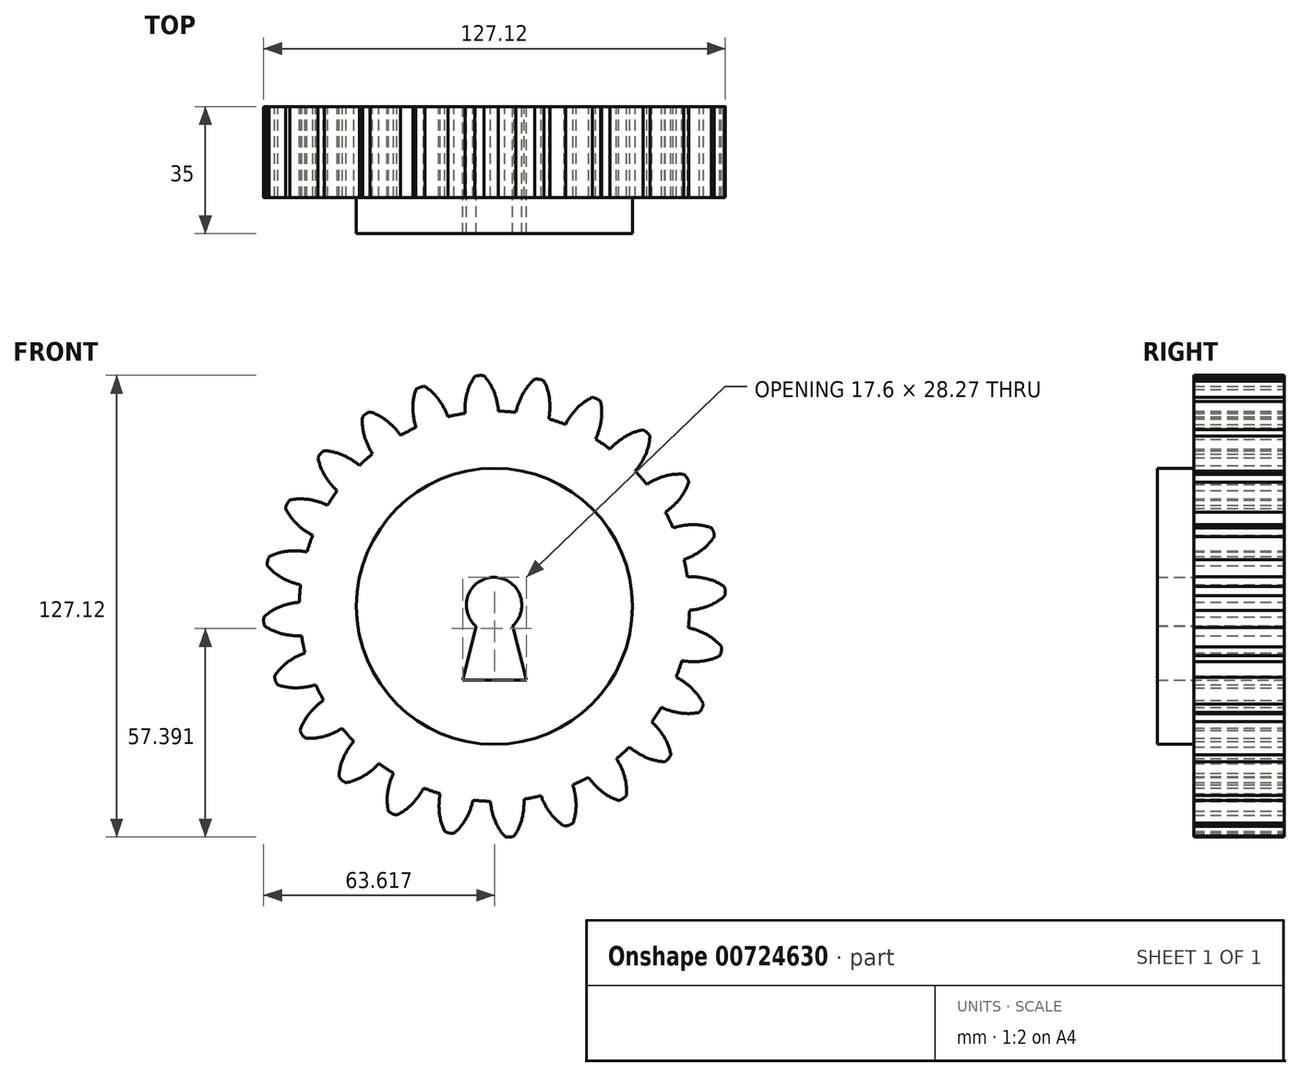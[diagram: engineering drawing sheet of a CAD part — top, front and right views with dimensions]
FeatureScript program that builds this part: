
annotation { "Feature Type Name" : "Feature", "Feature Type Description" : "" }
export const myFeature = defineFeature(function(context is Context, id is Id, definition is map)
    precondition{}
    {
        {
            var Q0;
            Q0=qCreatedBy(makeId("Front.planeOp"),FACE);
            var sketch = newSketch(context, id + "F0", { "sketchPlane" : qUnion([Q0])});
            skCircle(sketch, "E0", {"center": v(0, 0) * mm, "radius": 53.72 * mm});
            skCircle(sketch, "E1", {"center": v(0, 0) * mm, "radius": 58.67 * mm, "construction": true});
            skCircle(sketch, "E2", {"center": v(0, 0) * mm, "radius": 63.5 * mm, "construction": true});
            skLineSegment(sketch, "E3", {"start": v(0, 0) * mm, "end": v(0, 91.84) * mm, "construction": true});
            skLineSegment(sketch, "E4", {"start": v(0, 0) * mm, "end": v(-7.41, 113.09) * mm, "construction": true});
            skLineSegment(sketch, "E5", {"start": v(0, 58.67) * mm, "end": v(-83.5, 56.59) * mm, "construction": true});
            skLineSegment(sketch, "E6", {"start": v(0, 58.67) * mm, "end": v(-75.39, 29.08) * mm, "construction": true});
            skCircle(sketch, "E7", {"center": v(0, 0) * mm, "radius": 54.62 * mm, "construction": true});
            skCircle(sketch, "E8", {"center": v(0, 58.67) * mm, "radius": 16.52 * mm, "construction": true});
            skCircle(sketch, "E9", {"center": v(-15.38, 52.64) * mm, "radius": 16.52 * mm, "construction": true});
            skArc(sketch, "E10", {"start": v(0, 58.67) * mm, "mid": v(-1.21, 61.19) * mm, "end": v(-2.87, 63.43) * mm});
            skArc(sketch, "E11", {"start": v(1.1, 53.7) * mm, "mid": v(0.72, 56.23) * mm, "end": v(0, 58.67) * mm});
            skArc(sketch, "E12.MirrorCS", {"start": v(-8.1, 53.1) * mm, "mid": v(-8.06, 55.65) * mm, "end": v(-7.66, 58.17) * mm});
            skArc(sketch, "E13.MirrorCS", {"start": v(-7.66, 58.17) * mm, "mid": v(-6.78, 60.82) * mm, "end": v(-5.43, 63.27) * mm});
            skArc(sketch, "E14", {"start": v(-2.87, 63.43) * mm, "mid": v(-4.17, 63.55) * mm, "end": v(-5.43, 63.27) * mm});
            skCircle(sketch, "E15", {"center": v(-0.1, 0.31) * mm, "radius": 7.65 * mm});
            skLineSegment(sketch, "E16", {"start": v(-5.08, -5.5) * mm, "end": v(-8.74, -20.3) * mm});
            skLineSegment(sketch, "E17", {"start": v(-8.74, -20.3) * mm, "end": v(8.86, -20.3) * mm});
            skLineSegment(sketch, "E18", {"start": v(8.86, -20.3) * mm, "end": v(5.03, -5.36) * mm});
            skCircle(sketch, "E19", {"center": v(0, 0) * mm, "radius": 38.01 * mm});
            skSolve(sketch);
        }
        {
            var Q0;
            Q0=makeQuery(id+"F0.imprint","IMPRINT",FACE,{"disambiguationData":[TD([[makeQuery(id+"F0.imprint","IMPRINT",EDGE,{"derivedFrom":sQuery(id+"F0.wireOp",EDGE,"E19")}),-1.0]])]});
            var Q1;
            Q1=makeQuery(id+"F0.imprint","IMPRINT",FACE,{"disambiguationData":[TD([[makeQuery(id+"F0.imprint","IMPRINT",EDGE,{"derivedFrom":sQuery(id+"F0.wireOp",EDGE,"E10")}),1.0]])]});
            extrude(context, id + "F1", {"entities" : qUnion([Q0, Q1]), "depth" : 25 * mm, "offsetDistance" : 25 * mm});
        }
        {
            var Q0;
            Q0=makeQuery(id+"F1.opExtrude","SWEPT_BODY",BODY,{"disambiguationData":[OSD([sQuery(id+"F0.wireOp",EDGE,"E0"),sQuery(id+"F0.wireOp",EDGE,"E10"),sQuery(id+"F0.wireOp",EDGE,"E11"),sQuery(id+"F0.wireOp",EDGE,"E12.MirrorCS"),sQuery(id+"F0.wireOp",EDGE,"E13.MirrorCS"),sQuery(id+"F0.wireOp",EDGE,"E14")])]});
            var Q1;
            Q1=makeQuery(id+"F1.opExtrude","SWEPT_FACE",FACE,{"disambiguationData":[OSD([sQuery(id+"F0.wireOp",EDGE,"E0")])]});
            circularPattern(context, id + "F2", {"entities" : qUnion([Q0]), "axis" : qUnion([Q1]), "angle" : 360 * degree, "instanceCount" : 24, "equalSpace" : true});
        }
        {
            var Q0;
            {var subQ1=sQuery(id+"F0.wireOp",EDGE,"E16");Q0=makeQuery(id+"F0.imprint","IMPRINT",FACE,{"disambiguationData":[TD([[makeQuery(id+"F0.imprint","IMPRINT",EDGE,{"derivedFrom":subQ1}),-1.0]])]});}
            extrude(context, id + "F3", {"entities" : qUnion([Q0]), "operationType" : NewBodyOperationType.ADD, "depth" : 35 * mm, "offsetDistance" : 25 * mm});
        }
    });
